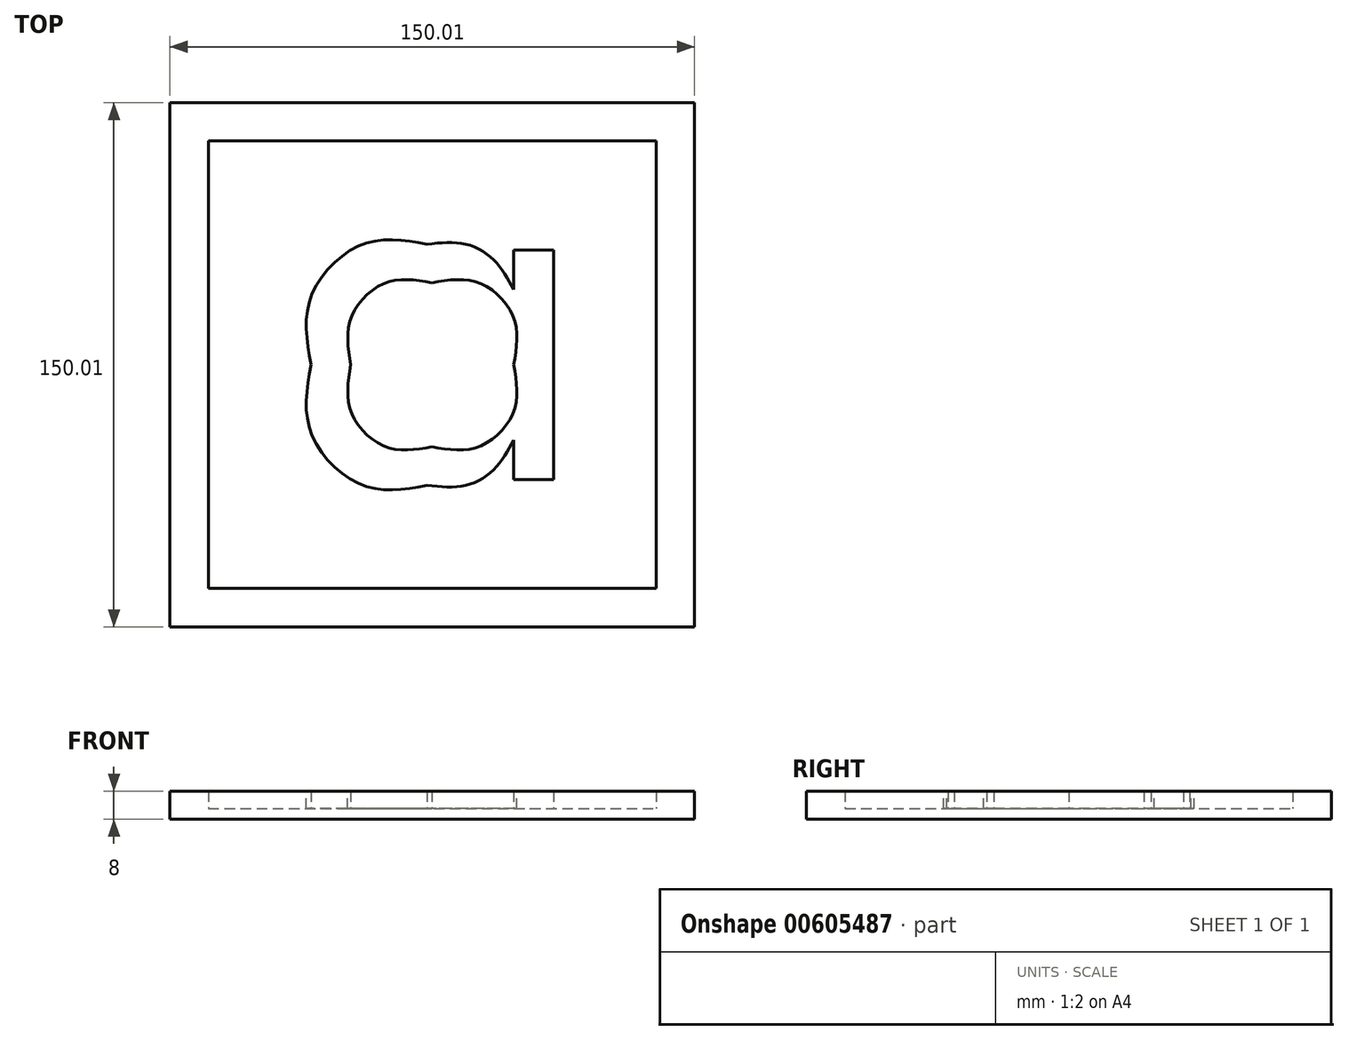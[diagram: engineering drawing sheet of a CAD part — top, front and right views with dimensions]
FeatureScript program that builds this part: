
annotation { "Feature Type Name" : "Feature", "Feature Type Description" : "" }
export const myFeature = defineFeature(function(context is Context, id is Id, definition is map)
    precondition{}
    {
        {
            var Q0;
            Q0=qCreatedBy(makeId("Top.planeOp"),FACE);
            var sketch = newSketch(context, id + "F0", { "sketchPlane" : qUnion([Q0])});
            skLineSegment(sketch, "E0", {"start": v(-75, -75.01) * mm, "end": v(75, -75.01) * mm});
            skLineSegment(sketch, "E1", {"start": v(75.01, -75) * mm, "end": v(75.01, 75) * mm});
            skLineSegment(sketch, "E2", {"start": v(75, 75.01) * mm, "end": v(-75, 75.01) * mm});
            skLineSegment(sketch, "E3", {"start": v(-75.01, 75) * mm, "end": v(-75.01, -75) * mm});
            skFitSpline(sketch, "E4", {"points": [v(23.29, 0) * mm, v(23.29, 13.38) * mm, v(13.18, 23.48) * mm, v(-0.07, 23.48) * mm]});
            skFitSpline(sketch, "E5", {"points": [v(-0.07, 23.48) * mm, v(-13.18, 23.48) * mm, v(-23.29, 13.38) * mm, v(-23.29, 0) * mm]});
            skFitSpline(sketch, "E6", {"points": [v(-23.29, 0) * mm, v(-23.29, -13.38) * mm, v(-13.18, -23.48) * mm, v(-0.07, -23.48) * mm]});
            skFitSpline(sketch, "E7", {"points": [v(-0.07, -23.48) * mm, v(13.18, -23.48) * mm, v(23.29, -13.38) * mm, v(23.29, 0) * mm]});
            skLineSegment(sketch, "E8", {"start": v(34.7, 32.8) * mm, "end": v(34.7, -32.8) * mm});
            skLineSegment(sketch, "E9", {"start": v(34.7, -32.8) * mm, "end": v(23.29, -32.8) * mm});
            skLineSegment(sketch, "E10", {"start": v(23.29, -32.8) * mm, "end": v(23.29, -21.51) * mm});
            skFitSpline(sketch, "E11", {"points": [v(23.29, -21.51) * mm, v(18.04, -29.52) * mm, v(9.64, -34.5) * mm, v(-1.5, -34.5) * mm]});
            skFitSpline(sketch, "E12", {"points": [v(-1.5, -34.5) * mm, v(-19.74, -34.5) * mm, v(-34.7, -19.42) * mm, v(-34.7, 0) * mm]});
            skFitSpline(sketch, "E13", {"points": [v(-34.7, 0) * mm, v(-34.7, 19.42) * mm, v(-19.74, 34.5) * mm, v(-1.5, 34.5) * mm]});
            skFitSpline(sketch, "E14", {"points": [v(-1.5, 34.5) * mm, v(9.64, 34.5) * mm, v(18.04, 29.52) * mm, v(23.29, 21.51) * mm]});
            skLineSegment(sketch, "E15", {"start": v(23.29, 21.51) * mm, "end": v(23.29, 32.8) * mm});
            skLineSegment(sketch, "E16", {"start": v(23.29, 32.8) * mm, "end": v(34.7, 32.8) * mm});
            skLineSegment(sketch, "E17.0", {"start": v(-64.01, 64.01) * mm, "end": v(-64.01, -64.01) * mm});
            skLineSegment(sketch, "E17.1", {"start": v(64.01, 64.01) * mm, "end": v(-64.01, 64.01) * mm});
            skLineSegment(sketch, "E17.2", {"start": v(64.01, -64.01) * mm, "end": v(64.01, 64.01) * mm});
            skLineSegment(sketch, "E17.3", {"start": v(-64.01, -64.01) * mm, "end": v(64.01, -64.01) * mm});
            skLineSegment(sketch, "E18.bottom", {"start": v(-75, 75.01) * mm, "end": v(75.01, 75.01) * mm});
            skLineSegment(sketch, "E18.top", {"start": v(-75, -75) * mm, "end": v(75.01, -75) * mm});
            skLineSegment(sketch, "E18.left", {"start": v(-75, 75.01) * mm, "end": v(-75, -75) * mm});
            skLineSegment(sketch, "E18.right", {"start": v(75.01, 75.01) * mm, "end": v(75.01, -75) * mm});
            skSolve(sketch);
        }
        {
            var Q0;
            Q0=makeQuery(id+"F0.imprint","IMPRINT",FACE,{"disambiguationData":[TD([[makeQuery(id+"F0.imprint","IMPRINT",EDGE,{"derivedFrom":sQuery(id+"F0.wireOp",EDGE,"E17.0")}),-1.0]])]});
            var Q1;
            Q1=makeQuery(id+"F0.imprint","IMPRINT",FACE,{"disambiguationData":[TD([[makeQuery(id+"F0.imprint","IMPRINT",EDGE,{"derivedFrom":sQuery(id+"F0.wireOp",EDGE,"E8")}),1.0]])]});
            var Q2;
            Q2=makeQuery(id+"F0.imprint","IMPRINT",FACE,{"disambiguationData":[TD([[makeQuery(id+"F0.imprint","IMPRINT",EDGE,{"derivedFrom":sQuery(id+"F0.wireOp",EDGE,"E4")}),-1.0]])]});
            var Q3;
            Q3=makeQuery(id+"F0.imprint","IMPRINT",FACE,{"disambiguationData":[TD([[makeQuery(id+"F0.imprint","IMPRINT",EDGE,{"derivedFrom":sQuery(id+"F0.wireOp",EDGE,"E4")}),1.0]])]});
            extrude(context, id + "F1", {"entities" : qUnion([Q0, Q1, Q2, Q3]), "depth" : 3 * mm, "offsetDistance" : 25 * mm});
        }
        {
            var Q0;
            Q0=makeQuery(id+"F0.imprint","IMPRINT",FACE,{"disambiguationData":[TD([[makeQuery(id+"F0.imprint","IMPRINT",EDGE,{"derivedFrom":sQuery(id+"F0.wireOp",EDGE,"E17.0")}),-1.0]])]});
            var Q1;
            Q1=makeQuery(id+"F0.imprint","IMPRINT",FACE,{"disambiguationData":[TD([[makeQuery(id+"F0.imprint","IMPRINT",EDGE,{"derivedFrom":sQuery(id+"F0.wireOp",EDGE,"E4")}),-1.0]])]});
            extrude(context, id + "F2", {"entities" : qUnion([Q0, Q1]), "operationType" : NewBodyOperationType.ADD, "depth" : 8 * mm, "offsetDistance" : 25 * mm});
        }
    });
